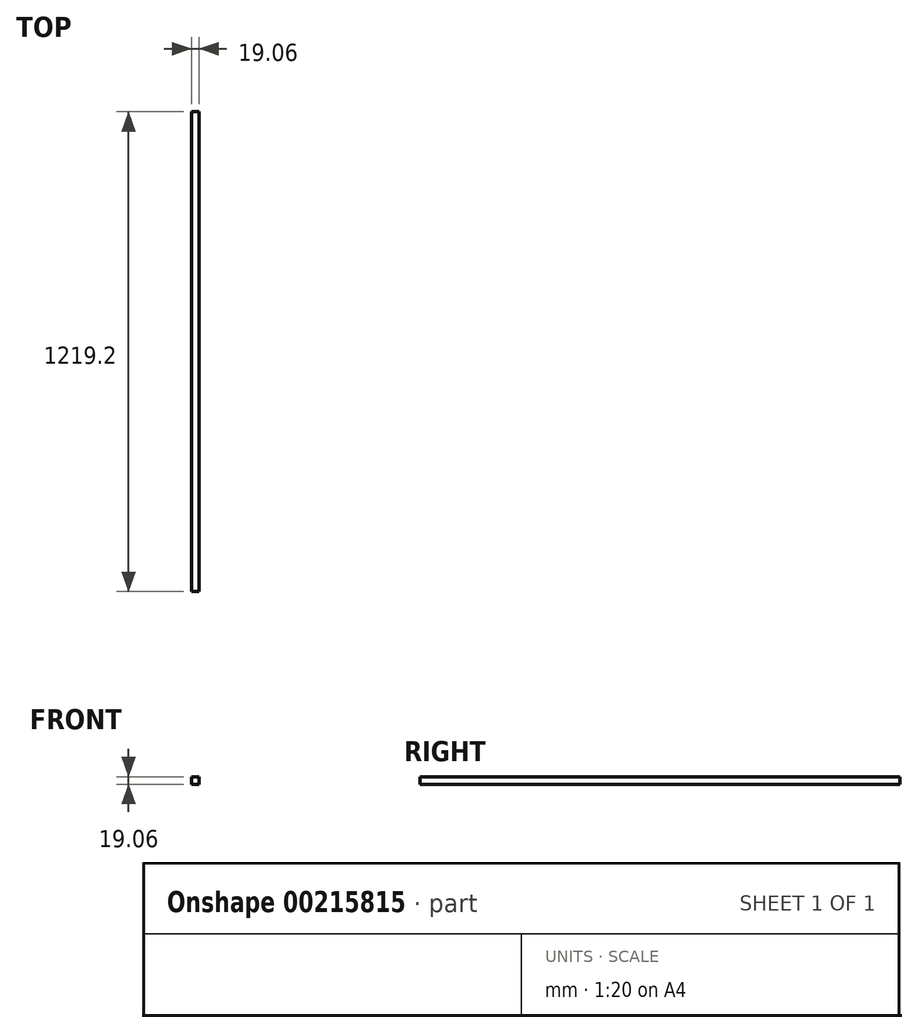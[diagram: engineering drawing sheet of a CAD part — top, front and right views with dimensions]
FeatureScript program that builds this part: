
annotation { "Feature Type Name" : "Feature", "Feature Type Description" : "" }
export const myFeature = defineFeature(function(context is Context, id is Id, definition is map)
    precondition{}
    {
        {
            var Q0;
            Q0=qCreatedBy(makeId("Front.planeOp"),FACE);
            var sketch = newSketch(context, id + "F0", { "sketchPlane" : qUnion([Q0])});
            skLineSegment(sketch, "E0.bottom", {"start": v(9.52, 9.53) * mm, "end": v(-9.53, 9.53) * mm});
            skLineSegment(sketch, "E0.top", {"start": v(9.53, -9.53) * mm, "end": v(-9.52, -9.53) * mm});
            skLineSegment(sketch, "E0.left", {"start": v(9.52, 9.53) * mm, "end": v(9.53, -9.53) * mm});
            skLineSegment(sketch, "E0.right", {"start": v(-9.53, 9.53) * mm, "end": v(-9.52, -9.53) * mm});
            skPoint(sketch, "E0.middle", {"position": v(0, 0) * mm});
            skSolve(sketch);
        }
        {
            var Q0;
            Q0 = qSketchRegion(id + "F0", true);
            extrude(context, id + "F1", {"entities" : qUnion([Q0]), "depth" : 609.6 * mm, "hasSecondDirection" : true, "secondDirectionOppositeDirection" : true, "secondDirectionDepth" : 609.6 * mm});
        }
    });
